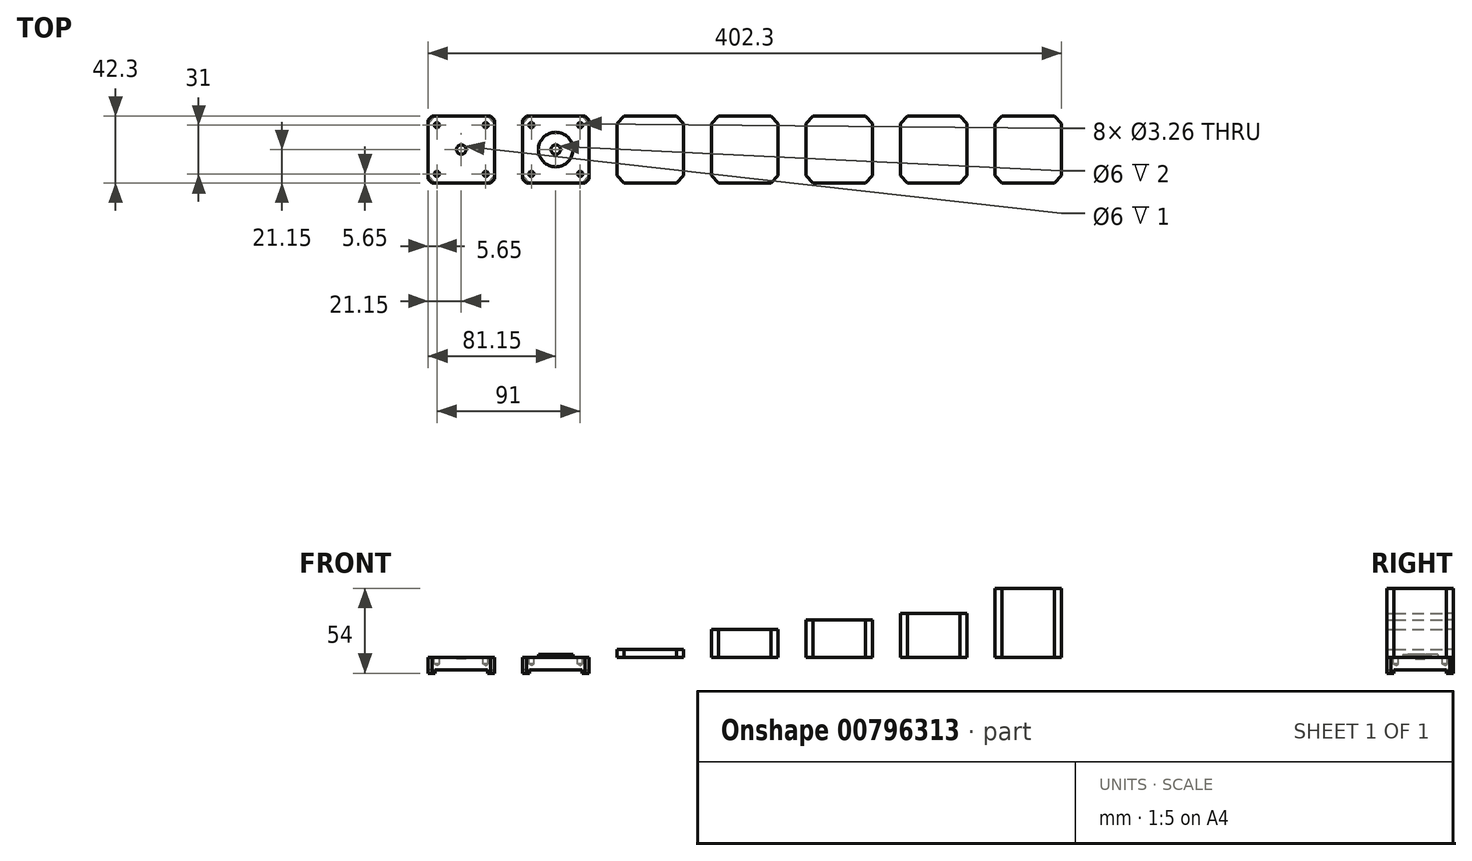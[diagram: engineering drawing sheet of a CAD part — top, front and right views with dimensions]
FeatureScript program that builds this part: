
annotation { "Feature Type Name" : "Feature", "Feature Type Description" : "" }
export const myFeature = defineFeature(function(context is Context, id is Id, definition is map)
    precondition{}
    {
        {
            var Q0;
            Q0=qCreatedBy(makeId("Top.planeOp"),FACE);
            var sketch = newSketch(context, id + "F0", { "sketchPlane" : qUnion([Q0])});
            skLineSegment(sketch, "E0.bottom", {"start": v(21.15, -21.15) * mm, "end": v(-21.15, -21.15) * mm});
            skLineSegment(sketch, "E0.top", {"start": v(21.15, 21.15) * mm, "end": v(-21.15, 21.15) * mm});
            skLineSegment(sketch, "E0.left", {"start": v(21.15, -21.15) * mm, "end": v(21.15, 21.15) * mm});
            skLineSegment(sketch, "E0.right", {"start": v(-21.15, -21.15) * mm, "end": v(-21.15, 21.15) * mm});
            skLineSegment(sketch, "E1", {"start": v(21.15, 21.15) * mm, "end": v(-21.15, -21.15) * mm, "construction": true});
            skLineSegment(sketch, "E2", {"start": v(-21.15, 21.15) * mm, "end": v(21.15, -21.15) * mm, "construction": true});
            skPoint(sketch, "E3", {"position": v(0, 0) * mm});
            skLineSegment(sketch, "E4.left", {"start": v(-15.5, 15.5) * mm, "end": v(-15.5, -15.5) * mm, "construction": true});
            skLineSegment(sketch, "E5", {"start": v(-15.5, 15.5) * mm, "end": v(15.5, 15.5) * mm, "construction": true});
            skLineSegment(sketch, "E6", {"start": v(15.5, 15.5) * mm, "end": v(15.5, -15.5) * mm, "construction": true});
            skLineSegment(sketch, "E7", {"start": v(15.5, -15.5) * mm, "end": v(-15.5, -15.5) * mm, "construction": true});
            skCircle(sketch, "E8", {"center": v(0, 0) * mm, "radius": 11 * mm});
            skCircle(sketch, "E9", {"center": v(0, 0) * mm, "radius": 3 * mm});
            skLineSegment(sketch, "E10", {"start": v(-16.65, 21.15) * mm, "end": v(-21.15, 16.65) * mm});
            skLineSegment(sketch, "E11", {"start": v(-18.65, 21.15) * mm, "end": v(-21.15, 18.65) * mm});
            skLineSegment(sketch, "E12", {"start": v(0, 0) * mm, "end": v(-15.5, 0) * mm, "construction": true});
            skLineSegment(sketch, "E13", {"start": v(0, 0) * mm, "end": v(0, 15.5) * mm, "construction": true});
            skLineSegment(sketch, "E14.MirrorCS", {"start": v(-16.65, -21.15) * mm, "end": v(-21.15, -16.65) * mm});
            skLineSegment(sketch, "E15.MirrorCS", {"start": v(-18.65, -21.15) * mm, "end": v(-21.15, -18.65) * mm});
            skLineSegment(sketch, "E16.MirrorCS", {"start": v(16.65, 21.15) * mm, "end": v(21.15, 16.65) * mm});
            skLineSegment(sketch, "E17.MirrorCS", {"start": v(18.65, 21.15) * mm, "end": v(21.15, 18.65) * mm});
            skLineSegment(sketch, "E18.MirrorCS", {"start": v(16.65, -21.15) * mm, "end": v(21.15, -16.65) * mm});
            skLineSegment(sketch, "E19.MirrorCS", {"start": v(18.65, -21.15) * mm, "end": v(21.15, -18.65) * mm});
            skPoint(sketch, "E20", {"position": v(-15.5, 15.5) * mm});
            skPoint(sketch, "E21", {"position": v(15.5, -15.5) * mm});
            skPoint(sketch, "E22", {"position": v(15.5, 15.5) * mm});
            skPoint(sketch, "E23", {"position": v(-15.5, -15.5) * mm});
            skLineSegment(sketch, "E24.1.0.0", {"start": v(-60, 0) * mm, "end": v(-60, 15.5) * mm, "construction": true});
            skCircle(sketch, "E24.1.0.1", {"center": v(-60, 0) * mm, "radius": 3 * mm});
            skLineSegment(sketch, "E24.1.0.2", {"start": v(-81.15, -21.15) * mm, "end": v(-81.15, 21.15) * mm});
            skPoint(sketch, "E24.1.0.3", {"position": v(-75.5, -15.5) * mm});
            skLineSegment(sketch, "E24.1.0.4", {"start": v(-38.85, -21.15) * mm, "end": v(-81.15, -21.15) * mm});
            skLineSegment(sketch, "E24.1.0.5", {"start": v(-78.65, -21.15) * mm, "end": v(-81.15, -18.65) * mm});
            skLineSegment(sketch, "E24.1.0.6", {"start": v(-76.65, -21.15) * mm, "end": v(-81.15, -16.65) * mm});
            skLineSegment(sketch, "E24.1.0.7", {"start": v(-43.35, -21.15) * mm, "end": v(-38.85, -16.65) * mm});
            skLineSegment(sketch, "E24.1.0.8", {"start": v(-41.35, -21.15) * mm, "end": v(-38.85, -18.65) * mm});
            skLineSegment(sketch, "E24.1.0.9", {"start": v(-38.85, -21.15) * mm, "end": v(-38.85, 21.15) * mm});
            skLineSegment(sketch, "E24.1.0.10", {"start": v(-43.35, 21.15) * mm, "end": v(-38.85, 16.65) * mm});
            skLineSegment(sketch, "E24.1.0.11", {"start": v(-41.35, 21.15) * mm, "end": v(-38.85, 18.65) * mm});
            skLineSegment(sketch, "E24.1.0.12", {"start": v(-38.85, 21.15) * mm, "end": v(-81.15, 21.15) * mm});
            skLineSegment(sketch, "E24.1.0.13", {"start": v(-76.65, 21.15) * mm, "end": v(-81.15, 16.65) * mm});
            skLineSegment(sketch, "E24.1.0.14", {"start": v(-78.65, 21.15) * mm, "end": v(-81.15, 18.65) * mm});
            skPoint(sketch, "E24.1.0.15", {"position": v(-75.5, 15.5) * mm});
            skPoint(sketch, "E24.1.0.16", {"position": v(-44.5, 15.5) * mm});
            skPoint(sketch, "E24.1.0.17", {"position": v(-44.5, -15.5) * mm});
            skLineSegment(sketch, "E24.direction1", {"start": v(0, 0) * mm, "end": v(-60, 0) * mm, "construction": true});
            skLineSegment(sketch, "E25.1.0.0", {"start": v(60, 0) * mm, "end": v(60, 15.5) * mm, "construction": true});
            skLineSegment(sketch, "E25.1.0.1", {"start": v(76.65, -21.15) * mm, "end": v(81.15, -16.65) * mm});
            skLineSegment(sketch, "E25.1.0.2", {"start": v(81.15, -21.15) * mm, "end": v(81.15, 21.15) * mm});
            skLineSegment(sketch, "E25.1.0.3", {"start": v(76.65, 21.15) * mm, "end": v(81.15, 16.65) * mm});
            skLineSegment(sketch, "E25.1.0.4", {"start": v(81.15, -21.15) * mm, "end": v(38.85, -21.15) * mm});
            skLineSegment(sketch, "E25.1.0.5", {"start": v(43.35, -21.15) * mm, "end": v(38.85, -16.65) * mm});
            skLineSegment(sketch, "E25.1.0.6", {"start": v(43.35, 21.15) * mm, "end": v(38.85, 16.65) * mm});
            skLineSegment(sketch, "E25.1.0.7", {"start": v(38.85, -21.15) * mm, "end": v(38.85, 21.15) * mm});
            skLineSegment(sketch, "E25.1.0.8", {"start": v(81.15, 21.15) * mm, "end": v(38.85, 21.15) * mm});
            skLineSegment(sketch, "E25.2.0.0", {"start": v(120, 0) * mm, "end": v(120, 15.5) * mm, "construction": true});
            skLineSegment(sketch, "E25.2.0.1", {"start": v(136.65, -21.15) * mm, "end": v(141.15, -16.65) * mm});
            skLineSegment(sketch, "E25.2.0.2", {"start": v(141.15, -21.15) * mm, "end": v(141.15, 21.15) * mm});
            skLineSegment(sketch, "E25.2.0.3", {"start": v(136.65, 21.15) * mm, "end": v(141.15, 16.65) * mm});
            skLineSegment(sketch, "E25.2.0.4", {"start": v(141.15, -21.15) * mm, "end": v(98.85, -21.15) * mm});
            skLineSegment(sketch, "E25.2.0.5", {"start": v(103.35, -21.15) * mm, "end": v(98.85, -16.65) * mm});
            skLineSegment(sketch, "E25.2.0.6", {"start": v(103.35, 21.15) * mm, "end": v(98.85, 16.65) * mm});
            skLineSegment(sketch, "E25.2.0.7", {"start": v(98.85, -21.15) * mm, "end": v(98.85, 21.15) * mm});
            skLineSegment(sketch, "E25.2.0.8", {"start": v(141.15, 21.15) * mm, "end": v(98.85, 21.15) * mm});
            skLineSegment(sketch, "E25.direction1", {"start": v(0, 0) * mm, "end": v(60, 0) * mm, "construction": true});
            skLineSegment(sketch, "E26.0.3.0", {"start": v(180, 0) * mm, "end": v(180, 15.5) * mm, "construction": true});
            skLineSegment(sketch, "E26.3.3.0", {"start": v(196.65, -21.15) * mm, "end": v(201.15, -16.65) * mm});
            skLineSegment(sketch, "E26.6.3.0", {"start": v(201.15, -21.15) * mm, "end": v(201.15, 21.15) * mm});
            skLineSegment(sketch, "E26.9.3.0", {"start": v(196.65, 21.15) * mm, "end": v(201.15, 16.65) * mm});
            skLineSegment(sketch, "E26.12.3.0", {"start": v(201.15, -21.15) * mm, "end": v(158.85, -21.15) * mm});
            skLineSegment(sketch, "E26.15.3.0", {"start": v(163.35, -21.15) * mm, "end": v(158.85, -16.65) * mm});
            skLineSegment(sketch, "E26.18.3.0", {"start": v(163.35, 21.15) * mm, "end": v(158.85, 16.65) * mm});
            skLineSegment(sketch, "E26.21.3.0", {"start": v(158.85, -21.15) * mm, "end": v(158.85, 21.15) * mm});
            skLineSegment(sketch, "E26.24.3.0", {"start": v(201.15, 21.15) * mm, "end": v(158.85, 21.15) * mm});
            skLineSegment(sketch, "E27.0.4.0", {"start": v(240, 0) * mm, "end": v(240, 15.5) * mm, "construction": true});
            skLineSegment(sketch, "E27.3.4.0", {"start": v(256.65, -21.15) * mm, "end": v(261.15, -16.65) * mm});
            skLineSegment(sketch, "E27.6.4.0", {"start": v(261.15, -21.15) * mm, "end": v(261.15, 21.15) * mm});
            skLineSegment(sketch, "E27.9.4.0", {"start": v(256.65, 21.15) * mm, "end": v(261.15, 16.65) * mm});
            skLineSegment(sketch, "E27.12.4.0", {"start": v(261.15, -21.15) * mm, "end": v(218.85, -21.15) * mm});
            skLineSegment(sketch, "E27.15.4.0", {"start": v(223.35, -21.15) * mm, "end": v(218.85, -16.65) * mm});
            skLineSegment(sketch, "E27.18.4.0", {"start": v(223.35, 21.15) * mm, "end": v(218.85, 16.65) * mm});
            skLineSegment(sketch, "E27.21.4.0", {"start": v(218.85, -21.15) * mm, "end": v(218.85, 21.15) * mm});
            skLineSegment(sketch, "E27.24.4.0", {"start": v(261.15, 21.15) * mm, "end": v(218.85, 21.15) * mm});
            skCircle(sketch, "E28", {"center": v(0, -30) * mm, "radius": 2.5 * mm});
            skCircle(sketch, "E29", {"center": v(0, -40) * mm, "radius": 2.5 * mm});
            skLineSegment(sketch, "E30", {"start": v(1.5, -42) * mm, "end": v(-1.5, -42) * mm});
            skLineSegment(sketch, "E31", {"start": v(1.5, -32) * mm, "end": v(-1.5, -32) * mm});
            skCircle(sketch, "E32.1.0.0", {"center": v(25, -40) * mm, "radius": 2.5 * mm});
            skCircle(sketch, "E32.1.0.1", {"center": v(25, -30) * mm, "radius": 2.5 * mm});
            skLineSegment(sketch, "E32.1.0.2", {"start": v(26.5, -32) * mm, "end": v(23.5, -32) * mm});
            skLineSegment(sketch, "E32.1.0.3", {"start": v(26.5, -42) * mm, "end": v(23.5, -42) * mm});
            skCircle(sketch, "E32.2.0.0", {"center": v(50, -40) * mm, "radius": 2.5 * mm});
            skCircle(sketch, "E32.2.0.1", {"center": v(50, -30) * mm, "radius": 2.5 * mm});
            skLineSegment(sketch, "E32.2.0.2", {"start": v(51.5, -32) * mm, "end": v(48.5, -32) * mm});
            skLineSegment(sketch, "E32.2.0.3", {"start": v(51.5, -42) * mm, "end": v(48.5, -42) * mm});
            skCircle(sketch, "E32.3.0.0", {"center": v(75, -40) * mm, "radius": 2.5 * mm});
            skCircle(sketch, "E32.3.0.1", {"center": v(75, -30) * mm, "radius": 2.5 * mm});
            skLineSegment(sketch, "E32.3.0.2", {"start": v(76.5, -32) * mm, "end": v(73.5, -32) * mm});
            skLineSegment(sketch, "E32.3.0.3", {"start": v(76.5, -42) * mm, "end": v(73.5, -42) * mm});
            skCircle(sketch, "E32.4.0.0", {"center": v(100, -40) * mm, "radius": 2.5 * mm});
            skCircle(sketch, "E32.4.0.1", {"center": v(100, -30) * mm, "radius": 2.5 * mm});
            skLineSegment(sketch, "E32.4.0.2", {"start": v(101.5, -32) * mm, "end": v(98.5, -32) * mm});
            skLineSegment(sketch, "E32.4.0.3", {"start": v(101.5, -42) * mm, "end": v(98.5, -42) * mm});
            skLineSegment(sketch, "E32.direction1", {"start": v(0, -40) * mm, "end": v(25, -40) * mm, "construction": true});
            skLineSegment(sketch, "E33.0.5.0", {"start": v(300, 0) * mm, "end": v(300, 15.5) * mm, "construction": true});
            skLineSegment(sketch, "E33.3.5.0", {"start": v(316.65, -21.15) * mm, "end": v(321.15, -16.65) * mm});
            skLineSegment(sketch, "E33.6.5.0", {"start": v(321.15, -21.15) * mm, "end": v(321.15, 21.15) * mm});
            skLineSegment(sketch, "E33.9.5.0", {"start": v(316.65, 21.15) * mm, "end": v(321.15, 16.65) * mm});
            skLineSegment(sketch, "E33.12.5.0", {"start": v(321.15, -21.15) * mm, "end": v(278.85, -21.15) * mm});
            skLineSegment(sketch, "E33.15.5.0", {"start": v(283.35, -21.15) * mm, "end": v(278.85, -16.65) * mm});
            skLineSegment(sketch, "E33.18.5.0", {"start": v(283.35, 21.15) * mm, "end": v(278.85, 16.65) * mm});
            skLineSegment(sketch, "E33.21.5.0", {"start": v(278.85, -21.15) * mm, "end": v(278.85, 21.15) * mm});
            skLineSegment(sketch, "E33.24.5.0", {"start": v(321.15, 21.15) * mm, "end": v(278.85, 21.15) * mm});
            skSolve(sketch);
        }
        {
            var Q0;
            Q0=makeQuery(id+"F0.imprint","IMPRINT",FACE,{"disambiguationData":[TD([[makeQuery(id+"F0.imprint","IMPRINT",EDGE,{"derivedFrom":sQuery(id+"F0.wireOp",EDGE,"E24.1.0.1")}),-1.0]])]});
            var Q1;
            Q1=makeQuery(id+"F0.imprint","IMPRINT",FACE,{"disambiguationData":[TD([[makeQuery(id+"F0.imprint","IMPRINT",EDGE,{"derivedFrom":sQuery(id+"F0.wireOp",EDGE,"E8")}),-1.0]])]});
            var Q2;
            Q2=makeQuery(id+"F0.imprint","IMPRINT",FACE,{"disambiguationData":[TD([[makeQuery(id+"F0.imprint","IMPRINT",EDGE,{"derivedFrom":sQuery(id+"F0.wireOp",EDGE,"E8")}),1.0]])]});
            var Q3;
            {var subQ0=sQuery(id+"F0.wireOp",EDGE,"E24.1.0.10");Q3=makeQuery(id+"F0.imprint","IMPRINT",FACE,{"disambiguationData":[TD([[makeQuery(id+"F0.imprint","IMPRINT",EDGE,{"derivedFrom":subQ0}),1.0]])]});}
            var Q4;
            {var subQ0=sQuery(id+"F0.wireOp",EDGE,"E24.1.0.13");Q4=makeQuery(id+"F0.imprint","IMPRINT",FACE,{"disambiguationData":[TD([[makeQuery(id+"F0.imprint","IMPRINT",EDGE,{"derivedFrom":subQ0}),-1.0]])]});}
            var Q5;
            {var subQ0=sQuery(id+"F0.wireOp",EDGE,"E24.1.0.5");Q5=makeQuery(id+"F0.imprint","IMPRINT",FACE,{"disambiguationData":[TD([[makeQuery(id+"F0.imprint","IMPRINT",EDGE,{"derivedFrom":subQ0}),-1.0]])]});}
            var Q6;
            {var subQ0=sQuery(id+"F0.wireOp",EDGE,"E24.1.0.7");Q6=makeQuery(id+"F0.imprint","IMPRINT",FACE,{"disambiguationData":[TD([[makeQuery(id+"F0.imprint","IMPRINT",EDGE,{"derivedFrom":subQ0}),-1.0]])]});}
            var Q7;
            {var subQ0=sQuery(id+"F0.wireOp",EDGE,"E14.MirrorCS");Q7=makeQuery(id+"F0.imprint","IMPRINT",FACE,{"disambiguationData":[TD([[makeQuery(id+"F0.imprint","IMPRINT",EDGE,{"derivedFrom":subQ0}),1.0]])]});}
            var Q8;
            {var subQ0=sQuery(id+"F0.wireOp",EDGE,"E10");Q8=makeQuery(id+"F0.imprint","IMPRINT",FACE,{"disambiguationData":[TD([[makeQuery(id+"F0.imprint","IMPRINT",EDGE,{"derivedFrom":subQ0}),-1.0]])]});}
            var Q9;
            {var subQ0=sQuery(id+"F0.wireOp",EDGE,"E16.MirrorCS");Q9=makeQuery(id+"F0.imprint","IMPRINT",FACE,{"disambiguationData":[TD([[makeQuery(id+"F0.imprint","IMPRINT",EDGE,{"derivedFrom":subQ0}),1.0]])]});}
            var Q10;
            {var subQ0=sQuery(id+"F0.wireOp",EDGE,"E18.MirrorCS");Q10=makeQuery(id+"F0.imprint","IMPRINT",FACE,{"disambiguationData":[TD([[makeQuery(id+"F0.imprint","IMPRINT",EDGE,{"derivedFrom":subQ0}),-1.0]])]});}
            var Q11;
            Q11=makeQuery(id+"F0.imprint","IMPRINT",FACE,{"disambiguationData":[TD([[makeQuery(id+"F0.imprint","IMPRINT",EDGE,{"derivedFrom":sQuery(id+"F0.wireOp",EDGE,"E9")}),1.0]])]});
            var Q12;
            Q12=makeQuery(id+"F0.imprint","IMPRINT",FACE,{"disambiguationData":[TD([[makeQuery(id+"F0.imprint","IMPRINT",EDGE,{"derivedFrom":sQuery(id+"F0.wireOp",EDGE,"E24.1.0.1")}),1.0]])]});
            extrude(context, id + "F1", {"entities" : qUnion([Q0, Q1, Q2, Q3, Q4, Q5, Q6, Q7, Q8, Q9, Q10, Q11, Q12]), "oppositeDirection" : true, "depth" : 8 * mm, "offsetDistance" : 25 * mm});
        }
        {
            var Q0;
            Q0=makeQuery(id+"F0.imprint","IMPRINT",FACE,{"disambiguationData":[TD([[makeQuery(id+"F0.imprint","IMPRINT",EDGE,{"derivedFrom":sQuery(id+"F0.wireOp",EDGE,"E8")}),1.0]])]});
            extrude(context, id + "F2", {"entities" : qUnion([Q0]), "operationType" : NewBodyOperationType.ADD, "depth" : 2 * mm, "offsetDistance" : 25 * mm});
        }
        {
            var Q0;
            Q0=makeQuery(id+"F0.imprint","IMPRINT",FACE,{"disambiguationData":[TD([[makeQuery(id+"F0.imprint","IMPRINT",EDGE,{"derivedFrom":sQuery(id+"F0.wireOp",EDGE,"E24.1.0.1")}),1.0]])]});
            extrude(context, id + "F3", {"entities" : qUnion([Q0]), "operationType" : NewBodyOperationType.REMOVE, "oppositeDirection" : true, "depth" : 1 * mm, "offsetDistance" : 25 * mm});
        }
        {
            var Q0;
            Q0=makeQuery(id+"F1.opExtrude","CAP_FACE",FACE,{"disambiguationData":[OSD([sQuery(id+"F0.wireOp",EDGE,"E0.bottom"),sQuery(id+"F0.wireOp",EDGE,"E0.top"),sQuery(id+"F0.wireOp",EDGE,"E0.left"),sQuery(id+"F0.wireOp",EDGE,"E0.right"),sQuery(id+"F0.wireOp",EDGE,"E11"),sQuery(id+"F0.wireOp",EDGE,"E15.MirrorCS"),sQuery(id+"F0.wireOp",EDGE,"E17.MirrorCS"),sQuery(id+"F0.wireOp",EDGE,"E19.MirrorCS")])],"isStart":false});
            var sketch = newSketch(context, id + "F4", { "sketchPlane" : qUnion([Q0])});
            skLineSegment(sketch, "E34.0", {"start": v(16.65, -21.15) * mm, "end": v(21.15, -16.65) * mm});
            skLineSegment(sketch, "E34.1", {"start": v(18.65, -21.15) * mm, "end": v(21.15, -18.65) * mm});
            skLineSegment(sketch, "E34.2", {"start": v(21.15, 18.65) * mm, "end": v(21.15, 16.65) * mm});
            skLineSegment(sketch, "E34.3", {"start": v(18.65, -21.15) * mm, "end": v(16.65, -21.15) * mm});
            skLineSegment(sketch, "E34.4", {"start": v(-16.65, -21.15) * mm, "end": v(-21.15, -16.65) * mm});
            skLineSegment(sketch, "E34.5", {"start": v(-18.65, -21.15) * mm, "end": v(-21.15, -18.65) * mm});
            skLineSegment(sketch, "E34.6", {"start": v(-21.15, 18.65) * mm, "end": v(-21.15, 16.65) * mm});
            skLineSegment(sketch, "E34.7", {"start": v(18.65, 21.15) * mm, "end": v(21.15, 18.65) * mm});
            skLineSegment(sketch, "E34.8", {"start": v(16.65, 21.15) * mm, "end": v(21.15, 16.65) * mm});
            skLineSegment(sketch, "E34.9", {"start": v(18.65, 21.15) * mm, "end": v(16.65, 21.15) * mm});
            skLineSegment(sketch, "E34.10", {"start": v(-16.65, 21.15) * mm, "end": v(-21.15, 16.65) * mm});
            skLineSegment(sketch, "E34.11", {"start": v(-18.65, 21.15) * mm, "end": v(-21.15, 18.65) * mm});
            skPoint(sketch, "E35.orphan", {"position": v(21.15, -21.15) * mm});
            skPoint(sketch, "E36.orphan", {"position": v(-21.15, -21.15) * mm});
            skLineSegment(sketch, "E37.trimOffspring", {"start": v(-21.15, -16.65) * mm, "end": v(-21.15, -18.65) * mm});
            skLineSegment(sketch, "E38.trimOffspring", {"start": v(-16.65, 21.15) * mm, "end": v(-18.65, 21.15) * mm});
            skLineSegment(sketch, "E39.trimOffspring", {"start": v(21.15, -16.65) * mm, "end": v(21.15, -18.65) * mm});
            skPoint(sketch, "E40.orphan", {"position": v(21.15, 21.15) * mm});
            skLineSegment(sketch, "E41.trimOffspring", {"start": v(-16.65, -21.15) * mm, "end": v(-18.65, -21.15) * mm});
            skPoint(sketch, "E42.orphan", {"position": v(-21.15, 21.15) * mm});
            skLineSegment(sketch, "E43.0", {"start": v(-38.85, 18.65) * mm, "end": v(-38.85, 16.65) * mm});
            skLineSegment(sketch, "E43.1", {"start": v(-43.35, -21.15) * mm, "end": v(-38.85, -16.65) * mm});
            skLineSegment(sketch, "E43.2", {"start": v(-41.35, -21.15) * mm, "end": v(-38.85, -18.65) * mm});
            skLineSegment(sketch, "E43.3", {"start": v(-41.35, -21.15) * mm, "end": v(-43.35, -21.15) * mm});
            skLineSegment(sketch, "E43.4", {"start": v(-41.35, 21.15) * mm, "end": v(-38.85, 18.65) * mm});
            skLineSegment(sketch, "E43.5", {"start": v(-43.35, 21.15) * mm, "end": v(-38.85, 16.65) * mm});
            skLineSegment(sketch, "E43.6", {"start": v(-41.35, 21.15) * mm, "end": v(-78.65, 21.15) * mm});
            skLineSegment(sketch, "E43.7", {"start": v(-76.65, -21.15) * mm, "end": v(-81.15, -16.65) * mm});
            skLineSegment(sketch, "E43.8", {"start": v(-78.65, -21.15) * mm, "end": v(-81.15, -18.65) * mm});
            skLineSegment(sketch, "E43.9", {"start": v(-81.15, 18.65) * mm, "end": v(-81.15, 16.65) * mm});
            skLineSegment(sketch, "E43.10", {"start": v(-78.65, 21.15) * mm, "end": v(-81.15, 18.65) * mm});
            skLineSegment(sketch, "E43.11", {"start": v(-76.65, 21.15) * mm, "end": v(-81.15, 16.65) * mm});
            skPoint(sketch, "E44.orphan", {"position": v(-38.85, -21.15) * mm});
            skLineSegment(sketch, "E45.trimOffspring", {"start": v(-76.65, -21.15) * mm, "end": v(-78.65, -21.15) * mm});
            skPoint(sketch, "E46.orphan", {"position": v(-81.15, -21.15) * mm});
            skLineSegment(sketch, "E47.trimOffspring", {"start": v(-81.15, -16.65) * mm, "end": v(-81.15, -18.65) * mm});
            skLineSegment(sketch, "E48.trimOffspring", {"start": v(-38.85, -16.65) * mm, "end": v(-38.85, -18.65) * mm});
            skPoint(sketch, "E49.orphan", {"position": v(-38.85, 21.15) * mm});
            skPoint(sketch, "E50.orphan", {"position": v(-81.15, 21.15) * mm});
            skSolve(sketch);
        }
        {
            var Q0;
            Q0=makeQuery(id+"F4.imprint","IMPRINT",FACE,{"disambiguationData":[TD([[makeQuery(id+"F4.imprint","IMPRINT",EDGE,{"derivedFrom":sQuery(id+"F4.wireOp",EDGE,"E43.1")}),-1.0]])]});
            var Q1;
            Q1=makeQuery(id+"F4.imprint","IMPRINT",FACE,{"disambiguationData":[TD([[makeQuery(id+"F4.imprint","IMPRINT",EDGE,{"derivedFrom":sQuery(id+"F4.wireOp",EDGE,"E43.7")}),1.0]])]});
            var Q2;
            Q2=makeQuery(id+"F4.imprint","IMPRINT",FACE,{"disambiguationData":[TD([[makeQuery(id+"F4.imprint","IMPRINT",EDGE,{"derivedFrom":sQuery(id+"F4.wireOp",EDGE,"E43.9")}),1.0]])]});
            var Q3;
            Q3=makeQuery(id+"F4.imprint","IMPRINT",FACE,{"disambiguationData":[TD([[makeQuery(id+"F4.imprint","IMPRINT",EDGE,{"derivedFrom":sQuery(id+"F4.wireOp",EDGE,"E43.0")}),-1.0]])]});
            var Q4;
            Q4=makeQuery(id+"F4.imprint","IMPRINT",FACE,{"disambiguationData":[TD([[makeQuery(id+"F4.imprint","IMPRINT",EDGE,{"derivedFrom":sQuery(id+"F4.wireOp",EDGE,"E34.4")}),1.0]])]});
            var Q5;
            Q5=makeQuery(id+"F4.imprint","IMPRINT",FACE,{"disambiguationData":[TD([[makeQuery(id+"F4.imprint","IMPRINT",EDGE,{"derivedFrom":sQuery(id+"F4.wireOp",EDGE,"E34.0")}),-1.0]])]});
            var Q6;
            Q6=makeQuery(id+"F4.imprint","IMPRINT",FACE,{"disambiguationData":[TD([[makeQuery(id+"F4.imprint","IMPRINT",EDGE,{"derivedFrom":sQuery(id+"F4.wireOp",EDGE,"E34.2")}),-1.0]])]});
            var Q7;
            Q7=makeQuery(id+"F4.imprint","IMPRINT",FACE,{"disambiguationData":[TD([[makeQuery(id+"F4.imprint","IMPRINT",EDGE,{"derivedFrom":sQuery(id+"F4.wireOp",EDGE,"E34.6")}),1.0]])]});
            extrude(context, id + "F5", {"entities" : qUnion([Q0, Q1, Q2, Q3, Q4, Q5, Q6, Q7]), "operationType" : NewBodyOperationType.ADD, "depth" : 2 * mm, "offsetDistance" : 25 * mm});
        }
        {
            var Q0;
            Q0=sQuery(id+"F0.wireOp",VERTEX,"E23");
            var Q1;
            Q1=sQuery(id+"F0.wireOp",VERTEX,"E21");
            var Q2;
            Q2=sQuery(id+"F0.wireOp",VERTEX,"E22");
            var Q3;
            Q3=sQuery(id+"F0.wireOp",VERTEX,"E20");
            var Q4;
            Q4=sQuery(id+"F0.wireOp",VERTEX,"E24.1.0.17");
            var Q5;
            Q5=sQuery(id+"F0.wireOp",VERTEX,"E24.1.0.16");
            var Q6;
            Q6=sQuery(id+"F0.wireOp",VERTEX,"E24.1.0.15");
            var Q7;
            Q7=sQuery(id+"F0.wireOp",VERTEX,"E24.1.0.3");
            var Q8;
            Q8=makeQuery(id+"F1.opExtrude","SWEPT_BODY",BODY,{"disambiguationData":[OSD([sQuery(id+"F0.wireOp",EDGE,"E0.bottom"),sQuery(id+"F0.wireOp",EDGE,"E0.top"),sQuery(id+"F0.wireOp",EDGE,"E0.left"),sQuery(id+"F0.wireOp",EDGE,"E0.right"),sQuery(id+"F0.wireOp",EDGE,"E11"),sQuery(id+"F0.wireOp",EDGE,"E15.MirrorCS"),sQuery(id+"F0.wireOp",EDGE,"E17.MirrorCS"),sQuery(id+"F0.wireOp",EDGE,"E19.MirrorCS")])]});
            var Q9;
            Q9=makeQuery(id+"F1.opExtrude","SWEPT_BODY",BODY,{"disambiguationData":[OSD([sQuery(id+"F0.wireOp",EDGE,"E24.1.0.2"),sQuery(id+"F0.wireOp",EDGE,"E24.1.0.4"),sQuery(id+"F0.wireOp",EDGE,"E24.1.0.5"),sQuery(id+"F0.wireOp",EDGE,"E24.1.0.8"),sQuery(id+"F0.wireOp",EDGE,"E24.1.0.9"),sQuery(id+"F0.wireOp",EDGE,"E24.1.0.11"),sQuery(id+"F0.wireOp",EDGE,"E24.1.0.12"),sQuery(id+"F0.wireOp",EDGE,"E24.1.0.14")])]});
            hole(context, id + "F6", {"style" : HoleStyle.SIMPLE, "endStyle" : HoleEndStyle.BLIND, "standardTappedOrClearance" : lookupTablePath({ "standard" : "ANSI", "fit" : "Normal (ASME)", "size" : "#4", "type" : "Clearance" }), "standardBlindInLast" : lookupTablePath({ "fit" : "Free", "standard" : "ANSI", "size" : "#4", "type" : "Clearance" }), "holeDiameter" : 3.26 * mm, "majorDiameter" : 5 * mm, "holeDepth" : 4 * mm, "isTappedThrough" : true, "tappedDepth" : 3.5 * mm, "tapClearance" : 3, "locations" : qUnion([Q0, Q1, Q2, Q3, Q4, Q5, Q6, Q7]), "scope" : qUnion([Q8, Q9])});
        }
        {
            var Q0;
            {var subQ1=sQuery(id+"F0.wireOp",EDGE,"E25.1.0.1");Q0=makeQuery(id+"F0.imprint","IMPRINT",FACE,{"disambiguationData":[TD([[makeQuery(id+"F0.imprint","IMPRINT",EDGE,{"derivedFrom":subQ1}),1.0]])]});}
            extrude(context, id + "F7", {"entities" : qUnion([Q0]), "depth" : 5 * mm, "offsetDistance" : 25 * mm});
        }
        {
            var Q0;
            {var subQ1=sQuery(id+"F0.wireOp",EDGE,"E25.2.0.1");Q0=makeQuery(id+"F0.imprint","IMPRINT",FACE,{"disambiguationData":[TD([[makeQuery(id+"F0.imprint","IMPRINT",EDGE,{"derivedFrom":subQ1}),1.0]])]});}
            extrude(context, id + "F8", {"entities" : qUnion([Q0]), "depth" : 18 * mm, "offsetDistance" : 25 * mm});
        }
        {
            var Q0;
            {var subQ1=sQuery(id+"F0.wireOp",EDGE,"E26.3.3.0");Q0=makeQuery(id+"F0.imprint","IMPRINT",FACE,{"disambiguationData":[TD([[makeQuery(id+"F0.imprint","IMPRINT",EDGE,{"derivedFrom":subQ1}),1.0]])]});}
            extrude(context, id + "F9", {"entities" : qUnion([Q0]), "depth" : 24 * mm, "offsetDistance" : 25 * mm});
        }
        {
            var Q0;
            {var subQ1=sQuery(id+"F0.wireOp",EDGE,"E27.3.4.0");Q0=makeQuery(id+"F0.imprint","IMPRINT",FACE,{"disambiguationData":[TD([[makeQuery(id+"F0.imprint","IMPRINT",EDGE,{"derivedFrom":subQ1}),1.0]])]});}
            extrude(context, id + "F10", {"entities" : qUnion([Q0]), "depth" : 28 * mm, "offsetDistance" : 25 * mm});
        }
        {
            var Q0;
            {var subQ1=sQuery(id+"F0.wireOp",EDGE,"E33.3.5.0");Q0=makeQuery(id+"F0.imprint","IMPRINT",FACE,{"disambiguationData":[TD([[makeQuery(id+"F0.imprint","IMPRINT",EDGE,{"derivedFrom":subQ1}),1.0]])]});}
            extrude(context, id + "F11", {"entities" : qUnion([Q0]), "depth" : 44 * mm, "offsetDistance" : 25 * mm});
        }
    });
